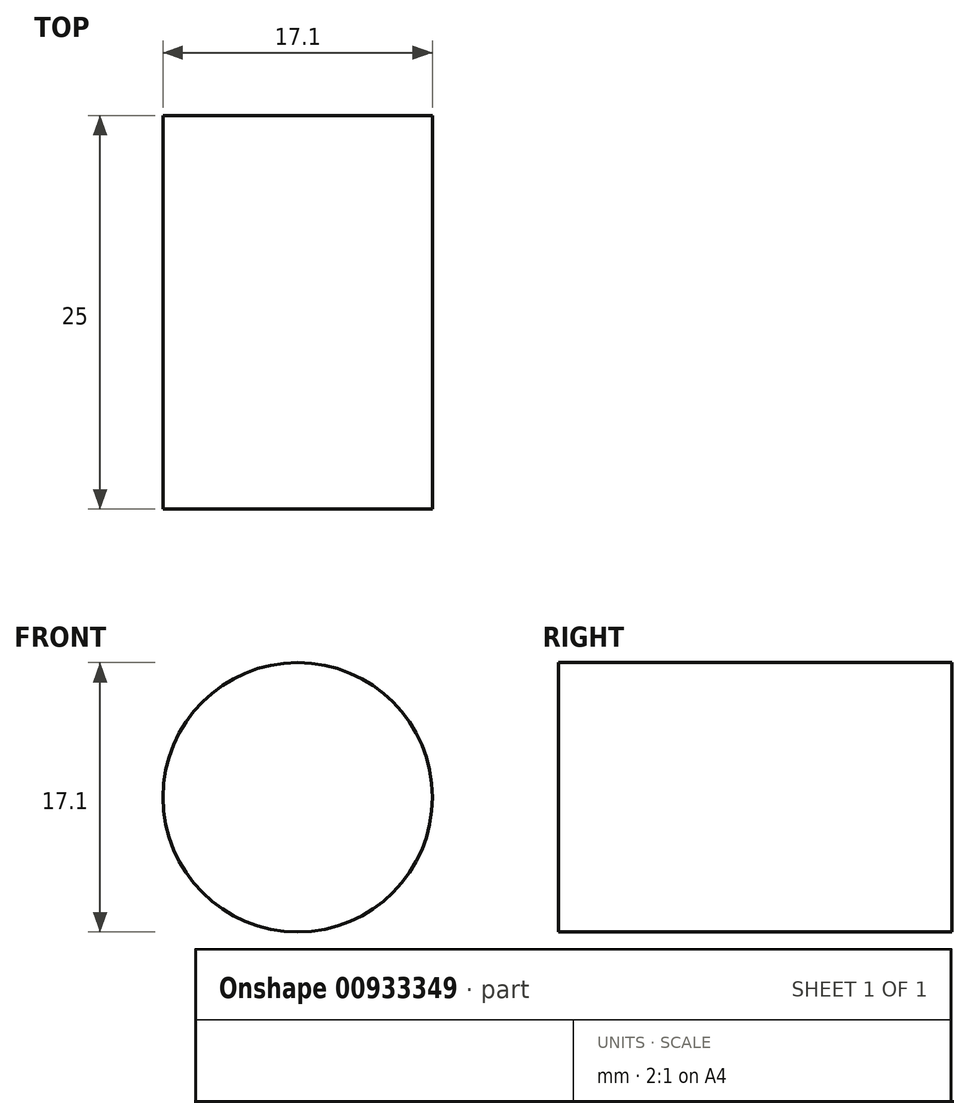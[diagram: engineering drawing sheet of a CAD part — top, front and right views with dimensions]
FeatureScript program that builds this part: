
annotation { "Feature Type Name" : "Feature", "Feature Type Description" : "" }
export const myFeature = defineFeature(function(context is Context, id is Id, definition is map)
    precondition{}
    {
        {
            var Q0;
            Q0=qCreatedBy(makeId("Front.planeOp"),FACE);
            var sketch = newSketch(context, id + "F0", { "sketchPlane" : qUnion([Q0])});
            skCircle(sketch, "E0", {"center": v(0, 0) * mm, "radius": 8.55 * mm});
            skLineSegment(sketch, "E1", {"start": v(0, -8.55) * mm, "end": v(22, -8.55) * mm});
            skLineSegment(sketch, "E2", {"start": v(0, -8.55) * mm, "end": v(-22, -8.55) * mm});
            skSolve(sketch);
        }
        {
            var Q0;
            Q0 = qSketchRegion(id + "F0", true);
            extrude(context, id + "F1", {"entities" : qUnion([Q0]), "depth" : 25 * mm, "offsetDistance" : 25 * mm});
        }
    });
